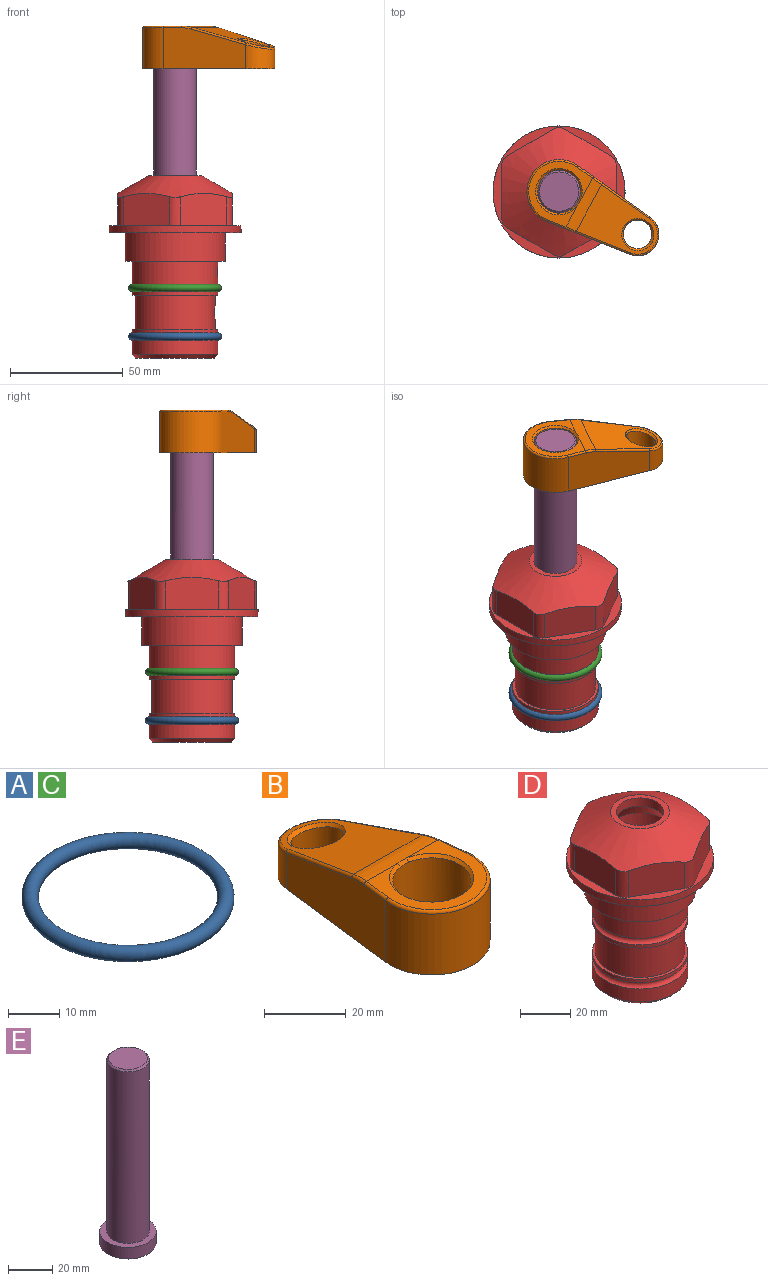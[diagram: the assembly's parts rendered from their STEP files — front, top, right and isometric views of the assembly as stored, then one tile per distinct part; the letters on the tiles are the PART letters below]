
ASSEMBLY  parts=5 mates=4
PART A: 1 faces, bbox 44.7x44.7x3.2 mm
  f0: torus R=19.05mm, axis (0,0,1), area 1193.9mm2
PART B: 31 faces, bbox 31.7x65.5x19.8 mm
  f0: plane 39.12x18.26mm, normal (0.99,0.12,0), area 612.2mm2, adj f1,f4,f7,f11,f13,f15
  f1: cylinder r=9.53mm len=18.91mm, axis (0,0,-1), area 296.1mm2, adj f0,f2,f7,f17
  f2: plane 39.12x18.26mm, normal (-0.99,0.12,0), area 612.2mm2, adj f1,f4,f7,f12,f14,f16
  f3: cylinder r=6.35mm len=12.7mm, axis (0,0,-1), area 362.4mm2, adj f7,f18
  f4: cylinder r=14.29mm len=28.58mm, axis (0,0,-1), area 882.2mm2, adj f0,f2,f7,f10
  f5: cylinder r=9.53mm len=19.05mm, axis (0,0,-1), area 1092.6mm2, adj f7,f19,f20
  f6: plane 26.99x23.69mm, normal (0,0,1), area 216.2mm2, adj f9,f10,f11,f12,f19
  f7: plane 63.5x28.58mm, normal (0,0,-1), area 661.8mm2, adj f0,f1,f2,f3,f4,f5,f22,f23
  f8: plane 33.52x23.6mm, normal (0,0.26,0.97), area 486mm2, adj f9,f15,f16,f17,f18
  f9: cylinder r=19.05mm len=24.72mm, axis (1,0,0), area 120.4mm2, adj f6,f8,f13,f14,f20
  f10: torus R=13.49mm, axis (0,0,1), area 59mm2, adj f4,f6,f11,f12
  f11: cylinder r=0.79mm len=8.67mm, axis (0.12,-0.99,0), area 10.8mm2, adj f0,f6,f10,f13
  f12: cylinder r=0.79mm len=8.67mm, axis (0.12,0.99,0), area 10.8mm2, adj f2,f6,f10,f14
  f13: bspline ~4.95x1.42mm, area 6.1mm2, adj f0,f9,f11,f15
  f14: bspline ~4.95x1.42mm, area 6.1mm2, adj f2,f9,f12,f16
  f15: cylinder r=0.79mm len=25.95mm, axis (0.12,-0.96,0.26), area 32.9mm2, adj f0,f8,f13,f17
  f16: cylinder r=0.79mm len=25.95mm, axis (0.12,0.96,-0.26), area 32.9mm2, adj f2,f8,f14,f17
  f17: bspline ~18.91x8.38mm, area 30mm2, adj f1,f8,f15,f16
  f18: bspline ~14.29x14.29mm, area 48.3mm2, adj f3,f8
  f19: cone r=9.53mm half-angle=45deg, axis (0,0,1), area 66.5mm2, adj f5,f6,f20
  f20: bspline ~3.22x0.96mm, area 3.5mm2, adj f5,f9,f19
  f21: plane 2.75x2.72mm, normal (0,0,-1), area 2.9mm2, adj f23,f25,f28
  f22: plane 23.05x15.88mm, normal (-0.99,-0.12,0), area 323.6mm2, adj f7,f25,f26,f27,f28,f29
  f23: plane 23.05x15.88mm, normal (0.99,-0.12,0), area 323.6mm2, adj f7,f21,f25,f27,f28,f30
  f24: cylinder r=9.53mm len=10.69mm, axis (0,0,-1), area 114.7mm2, adj f7,f27,f29,f30
  f25: cylinder r=12.7mm len=20.59mm, axis (0,0,-1), area 381.1mm2, adj f7,f21,f22,f23,f26,f28
  f26: plane 2.75x2.72mm, normal (0,0,-1), area 2.9mm2, adj f22,f25,f28
  f27: plane 19.72x18.37mm, normal (0,-0.26,-0.97), area 291.8mm2, adj f22,f23,f24,f28,f29,f30
  f28: cylinder r=15.88mm len=19.92mm, axis (1,0,0), area 54.8mm2, adj f21,f22,f23,f25,f26,f27
  f29: cylinder r=1.59mm len=11mm, axis (0,0,-1), area 34.7mm2, adj f7,f22,f24,f27
  f30: cylinder r=1.59mm len=11mm, axis (0,0,-1), area 34.7mm2, adj f7,f23,f24,f27
PART C: same geometry as A
PART D: 36 faces, bbox 58.7x58.7x81 mm
  f0: cylinder r=17.78mm len=35.56mm, axis (0,0,1), area 1670.8mm2, adj f23,f24,f31
  f1: cylinder r=19.05mm len=38.1mm, axis (0,0,1), area 1191.9mm2, adj f26,f27,f30
  f2: plane 58.66x58.66mm, normal (0,0,-1), area 1150.6mm2, adj f3,f28
  f3: cylinder r=29.33mm len=58.66mm, axis (0,0,-1), area 585.1mm2, adj f2,f4
  f4: plane 58.66x58.66mm, normal (0,0,1), area 475.9mm2, adj f3,f5,f6,f7,f8,f9,f10,f11
  f5: plane 20.32x14.34mm, normal (-0.5,0.87,0), area 324.4mm2, adj f4,f15,f16,f17
  f6: plane 20.32x14.34mm, normal (0.5,0.87,0), area 324.4mm2, adj f4,f14,f15,f17
  f7: plane 23.48x14.34mm, normal (1,0,0), area 324.4mm2, adj f4,f13,f14,f17
  f8: plane 20.32x14.34mm, normal (0.5,-0.87,0), area 324.4mm2, adj f4,f12,f13,f17
  f9: plane 20.32x14.34mm, normal (-0.5,-0.87,0), area 324.4mm2, adj f4,f11,f12,f17
  f10: plane 23.48x14.34mm, normal (-1,0,0), area 324.4mm2, adj f4,f11,f16,f17
  f11: cylinder r=5.08mm len=12.85mm, axis (0,0,-1), area 67.2mm2, adj f4,f9,f10,f17
  f12: cylinder r=5.08mm len=12.85mm, axis (0,0,-1), area 67.2mm2, adj f4,f8,f9,f17
  f13: cylinder r=5.08mm len=12.85mm, axis (0,0,-1), area 67.2mm2, adj f4,f7,f8,f17
  f14: cylinder r=5.08mm len=12.85mm, axis (0,0,-1), area 67.2mm2, adj f4,f6,f7,f17
  f15: cylinder r=5.08mm len=12.85mm, axis (0,0,-1), area 67.2mm2, adj f4,f5,f6,f17
  f16: cylinder r=5.08mm len=12.85mm, axis (0,0,-1), area 67.2mm2, adj f4,f5,f10,f17
  f17: cone r=11.73mm half-angle=60deg, axis (0,0,-1), area 2071.8mm2, adj f5,f6,f7,f8,f9,f10,f11,f12
  f18: plane 23.46x23.46mm, normal (0,0,1), area 147.4mm2, adj f17,f35
  f19: plane 34.93x34.93mm, normal (0,0,-1), area 958mm2, adj f29
  f20: cylinder r=19.05mm len=38.1mm, axis (0,0,1), area 760.1mm2, adj f21,f29
  f21: torus R=19.05mm, axis (0,0,1), area 565.3mm2, adj f20,f22
  f22: cylinder r=19.05mm len=38.1mm, axis (0,0,1), area 190mm2, adj f21,f23
  f23: plane 38.1x38.1mm, normal (0,0,1), area 146.9mm2, adj f0,f22
  f24: plane 38.1x38.1mm, normal (0,0,-1), area 146.9mm2, adj f0,f25
  f25: cylinder r=19.05mm len=38.1mm, axis (0,0,1), area 190mm2, adj f24,f26
  f26: torus R=19.05mm, axis (0,0,1), area 565.3mm2, adj f1,f25
  f27: plane 44.45x44.45mm, normal (0,0,-1), area 411.7mm2, adj f1,f28
  f28: cylinder r=22.23mm len=44.45mm, axis (0,0,1), area 1773.5mm2, adj f2,f27
  f29: cone r=19.05mm half-angle=45deg, axis (0,0,1), area 257.5mm2, adj f19,f20
  f30: cylinder r=3.17mm len=6.75mm, axis (-1,0,0), area 128mm2, adj f1,f33
  f31: cylinder r=3.17mm len=6.35mm, axis (-1,0,0), area 102.5mm2, adj f0,f33
  f32: plane 25.4x25.4mm, normal (0,0,1), area 506.7mm2, adj f33
  f33: cylinder r=12.7mm len=66.42mm, axis (0,0,-1), area 5236.2mm2, adj f30,f31,f32,f34
  f34: cone r=9.53mm half-angle=30deg, axis (0,0,-1), area 443.4mm2, adj f33,f35
  f35: cylinder r=9.53mm len=19.05mm, axis (0,0,-1), area 240.9mm2, adj f18,f34
PART E: 6 faces, bbox 25.4x25.4x101.6 mm
  f0: plane 17.46x17.46mm, normal (0,0,1), area 239.5mm2, adj f5
  f1: plane 25.4x25.4mm, normal (0,0,-1), area 506.7mm2, adj f2
  f2: cylinder r=12.7mm len=25.4mm, axis (0,0,1), area 506.7mm2, adj f1,f3
  f3: plane 25.4x25.4mm, normal (0,0,1), area 221.7mm2, adj f2,f4
  f4: cylinder r=9.53mm len=94.46mm, axis (0,0,1), area 5653mm2, adj f3,f5
  f5: cone r=8.73mm half-angle=45deg, axis (0,0,-1), area 64.4mm2, adj f0,f4
PLACE A t=(0,0,-21.59)mm
PLACE B rot(axis=(0,0,-1),118.5deg) t=(0,0,28.35)mm
PLACE C at identity
PLACE D at identity fixed
PLACE E rot(axis=(0,0,-1),118.5deg) t=(0,0,27.55)mm
MATE cylindrical E.f2 <-> D.f0  axis (0,0,-1) through (0,0,-10.55)mm
MATE fastened E.f2 <-> B.f4  axis (0,0,1) through (0,0,91.05)mm
MATE fastened C.f0 <-> D.f0  axis (0,0,1) through (0,0,-24.51)mm
MATE fastened A.f0 <-> D.f0  axis (0,0,1) through (0,0,-46.1)mm
